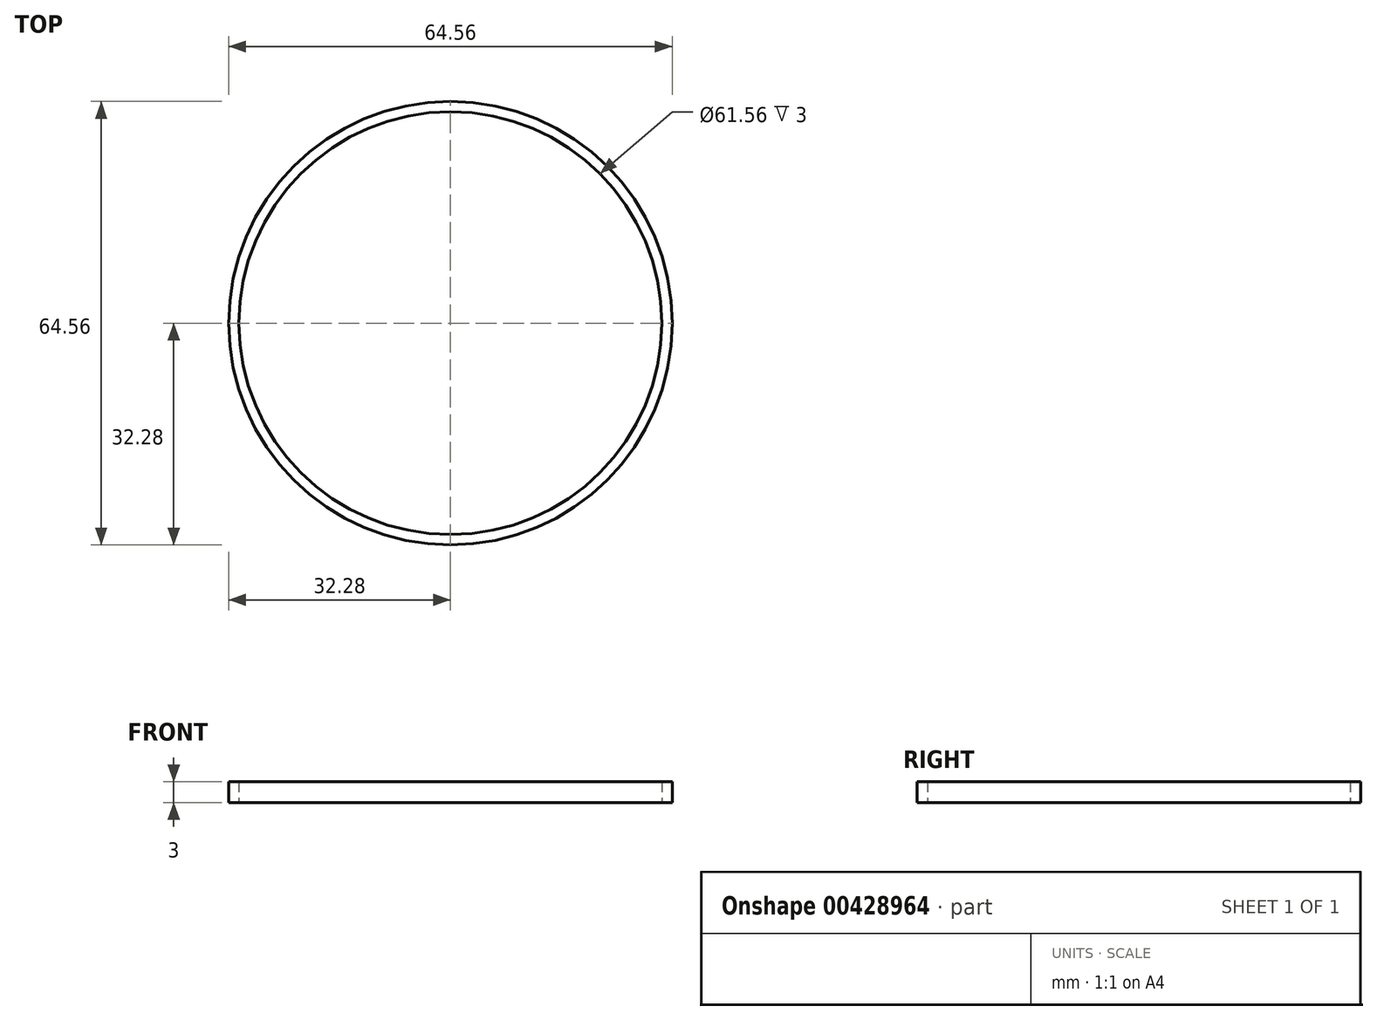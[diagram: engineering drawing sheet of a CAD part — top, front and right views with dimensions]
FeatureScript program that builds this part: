
annotation { "Feature Type Name" : "Feature", "Feature Type Description" : "" }
export const myFeature = defineFeature(function(context is Context, id is Id, definition is map)
    precondition{}
    {
        {
            var Q0;
            Q0=qCreatedBy(makeId("Top.planeOp"),FACE);
            var sketch = newSketch(context, id + "F0", { "sketchPlane" : qUnion([Q0])});
            skCircle(sketch, "E0", {"center": v(0, 0) * mm, "radius": 32.28 * mm});
            skCircle(sketch, "E1", {"center": v(0, 0) * mm, "radius": 30.78 * mm});
            skSolve(sketch);
        }
        {
            var Q0;
            Q0=makeQuery(id+"F0.imprint","IMPRINT",FACE,{"disambiguationData":[TD([[makeQuery(id+"F0.imprint","IMPRINT",EDGE,{"derivedFrom":sQuery(id+"F0.wireOp",EDGE,"E0")}),1.0]])]});
            extrude(context, id + "F1", {"entities" : qUnion([Q0]), "depth" : 3 * mm});
        }
    });
